# Revit family: IEK_РозеткаТелефонная_Встраиваемая_Одноместная IP20_КВАРТА
name_source: partatom
category: Устройства связи
units: mm (PartAtom-declared; Revit-internal decimal feet)

## family parameters
Всегда вертикально = Да
На основе рабочей плоскости = Нет
Общий = Нет
При загрузке вырезать с полостями = Нет
Размер круглого соединителя = Использовать диаметр
Сохранять ориентацию аннотаций = Да
Тип детали = Нормальный
Точка расчета площади = Нет

## types (2) — shared parameters
ADSK_URL страницы изделия = https://www.iek.ru
ADSK_Версия Revit = 2019
ADSK_Версия семейства = 1.0
ADSK_Группирование = III ЭЛЕКТРОУСТАНОВОЧНЫЕ И ЭЛЕКТРОМОНТАЖНЫЕ ИЗДЕЛИЯ
ADSK_Единица измерения = шт
ADSK_Завод-изготовитель = IEK
ADSK_Марка = КВАРТА
ADSK_Масса = 0.08
ADSK_Материал наименование = Пластик
IEK_URL = https://www.iek.ru
IEK_Описание = Классический дизайн, проверенный временем и востребованный различными категориями потребителей, позволяет устанавливать изделия серии "КВАРТА" в квартирах, загородных домах, офисных и производственных помещениях.
IEK_Цена за единицу = 163.12
KSI_CMa_Строительные материалы = 01.7.14.03
Высота = 81 мм
Глубина = 43 мм
Изготовитель = IEK
Степень защиты = IP20
Тип монтажа = Встраиваемый
Ширина = 82 мм

## per-type parameters (varying)
| type | ADSK_Код изделия | ADSK_Материал | ADSK_Наименование |
| РТ10-КБ | ETK10-K01-DM | Цвет белый | Розетка 1-местная телефонная РТ10-КБ КВАРТА белый IEK |
| РТ10-ККм | ETK10-K33-DM | Цвет кремовый | Розетка 1-местная телефонная РТ10-ККм КВАРТА кремовый IEK |
